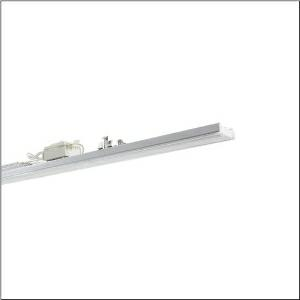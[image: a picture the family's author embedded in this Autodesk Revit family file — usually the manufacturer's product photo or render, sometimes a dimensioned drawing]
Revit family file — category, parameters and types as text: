
# Revit family: licross_r__11_recessed_ho_51te11dv4lxs_224b
name_source: partatom
category: Lighting Fixtures
units: mm (PartAtom-declared; Revit-internal decimal feet)

## family parameters
Cut with Voids When Loaded = No
Host = Face
Light Source = No
Part Type = Normal
Room Calculation Point = No
Round Connector Dimension = Use Diameter
Shared = No

## types (1)
- --- (1 x LED, 20300 lm, 108 W, 4000K)
    Apparent Load = 108 VA
    CIE Flux Codes = 87 95 99 100 100
    Color Rendering = 80
    Color Temperature = 4000K
    Default Elevation = 1800 mm
    Description = Licross® 11 Recessed HO, luminaire insert, of sheet steel, galvanised, coil coated, white, length: 2.250mm, width: 66mm, height: 67mm, LED rated luminous flux: 20.300lm, light colour: 840, control gear: DALI 2, with plug, 5-pole, with phase selection, mains connection: 220..240V, AC, 50/60Hz, rated input power: 108W, halogen-free wiring, primary light control with lens, of plastic, primary optical cover: cover, of PMMA, light emission: direct distribution, primary light characteristic: symmetric, protection rating (complete): IP54, insulation class (complete): insulation class I (protective earthing), certification: CE, ENEC, VDE, UKCA, protection symbol: D if used in an environment with non-conductive dust loads with corresponding accessories, impact resistance: IK06, permissible ambient temperature for indoor applications: -40..+45°C, corresponds to IFS (International Featured Standards) requirements for safety and quality in the food industry, reducing of maximum allowable ambient temperature of 5°C with ceiling mounting, LABS conformity tested according to VDMA 24364:2018-05, packaging unit: 1 piece
    Height = 58 mm
    Lamp = 1 x LED
    Lamp Light Flux = 20300 lm
    Lamp Power = 108 W
    Lamp count = 1
    Length = 2250 mm
    Luminous efficacy = 188 lm/W
    Manufacturer = Siteco
    ModVariant = No
    Model = 51TE11DV4LXS
    Mounting Place = Ceiling
    Mounting Type = Pendant
    Number of Poles = 1
    OnlyDefault = Yes
    Power Factor = 1
    Product Name = Licross® 11 Recessed HO
    Product group = luminaire insert
    ProductGroupID = 902
    Protection Class = Protection class I
    Protection Degree = IP 54
    RLX_Detail_Level = 1
    RLX_Emergency_Light_Flux = 0 lm
    RLX_Emergency_Type = 0
    RLX_Emergency_Type_DB = No
    RlxData = <blob elided: 29325 chars, md5=45954192>
    Socket = socket
    Standby Power = 0 W
    System Light Flux = 20300 lm
    System Power = 108 W
    Type Comments = factory setting: luminous flux: 100 % | dim-lin: 254 | 503 mA
    Type Image = l_1296930.jpg
    URL = http://relux.com
    VarID = @adj_082320
    Voltage = 0 V
    Weight = 0.00 kg
    Width = 66 mm

## geometry (parser evidence)
native form markers: Blend x4, Sweep x9
no freeform markers — native parametric forms only
